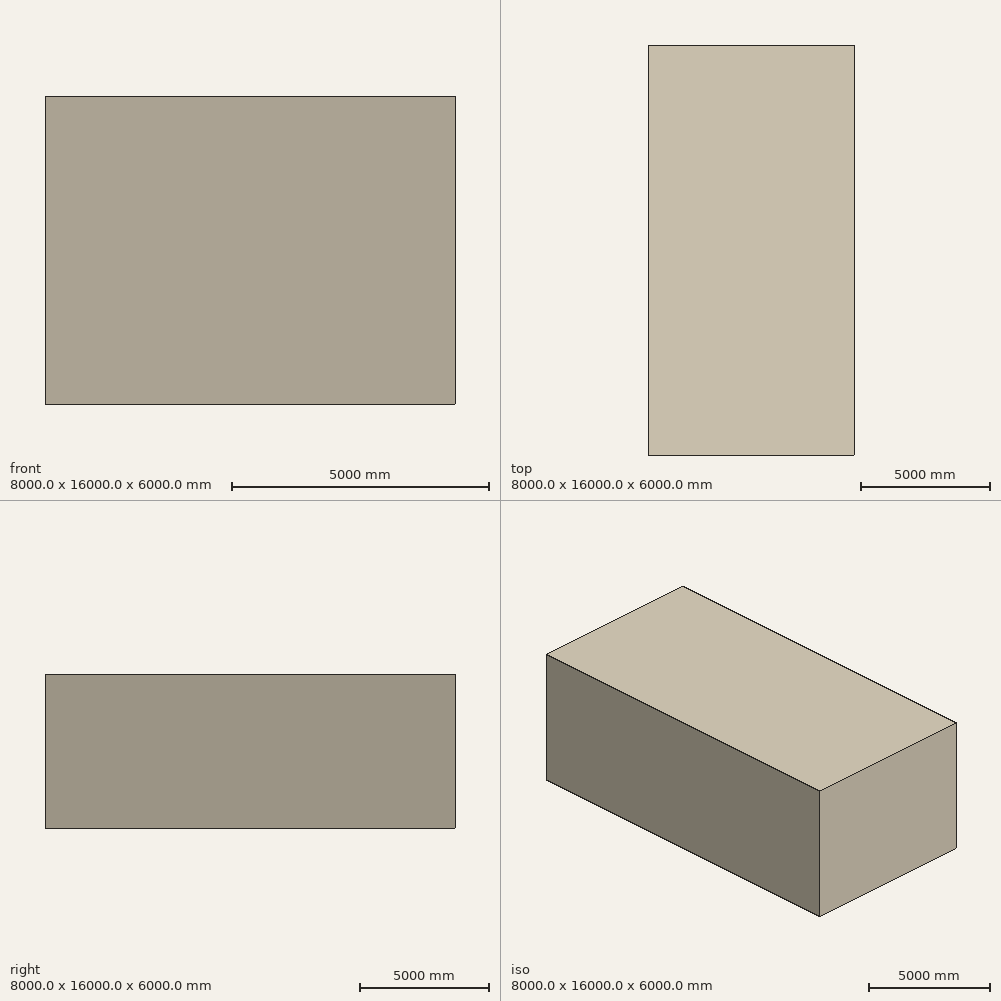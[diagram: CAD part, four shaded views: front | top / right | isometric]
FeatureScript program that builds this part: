
annotation { "Feature Type Name" : "Feature", "Feature Type Description" : "" }
export const myFeature = defineFeature(function(context is Context, id is Id, definition is map)
    precondition{}
    {
        {
            var Q0;
            Q0=qCreatedBy(makeId("Top.planeOp"),FACE);
            var sketch = newSketch(context, id + "F0", { "sketchPlane" : qUnion([Q0])});
            skLineSegment(sketch, "E0.bottom", {"start": v(0, 0) * mm, "end": v(8000, 0) * mm});
            skLineSegment(sketch, "E0.top", {"start": v(0, 16000) * mm, "end": v(8000, 16000) * mm});
            skLineSegment(sketch, "E0.left", {"start": v(0, 0) * mm, "end": v(0, 16000) * mm});
            skLineSegment(sketch, "E0.right", {"start": v(8000, 0) * mm, "end": v(8000, 16000) * mm});
            skSolve(sketch);
        }
        {
            var Q0;
            Q0=makeQuery(id+"F0.imprint","IMPRINT",FACE,{"disambiguationData":[TD([[makeQuery(id+"F0.imprint","IMPRINT",EDGE,{"derivedFrom":sQuery(id+"F0.wireOp",EDGE,"E0.bottom")}),1.0]])]});
            extrude(context, id + "F1", {"entities" : qUnion([Q0]), "depth" : 6000 * mm, "offsetDistance" : 25 * mm});
        }
    });
